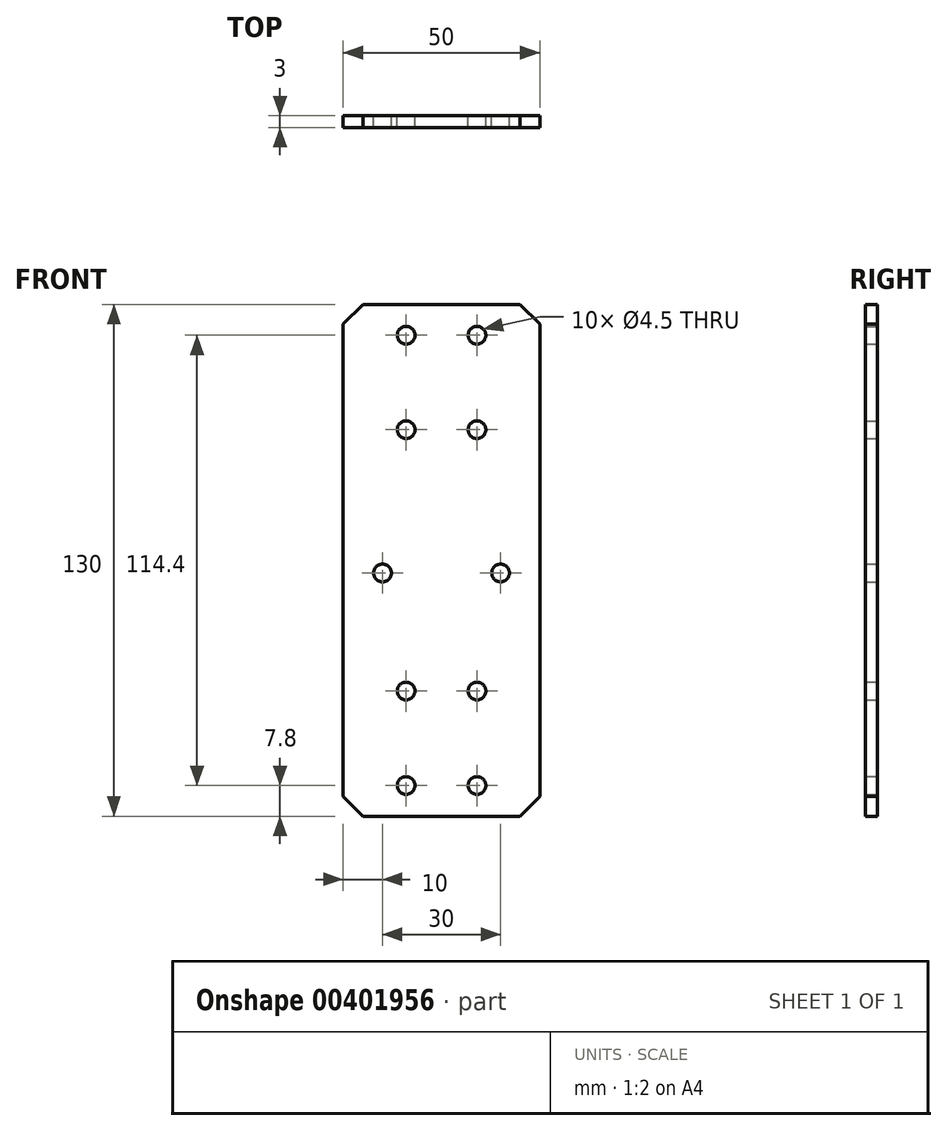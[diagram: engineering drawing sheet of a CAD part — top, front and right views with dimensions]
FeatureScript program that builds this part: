
annotation { "Feature Type Name" : "Feature", "Feature Type Description" : "" }
export const myFeature = defineFeature(function(context is Context, id is Id, definition is map)
    precondition{}
    {
        {
            var Q0;
            Q0=qCreatedBy(makeId("Front.planeOp"),FACE);
            var sketch = newSketch(context, id + "F0", { "sketchPlane" : qUnion([Q0])});
            skLineSegment(sketch, "E0.bottom", {"start": v(0, 0) * mm, "end": v(50, 0) * mm});
            skLineSegment(sketch, "E0.top", {"start": v(0, 130) * mm, "end": v(50, 130) * mm});
            skLineSegment(sketch, "E0.left", {"start": v(0, 0) * mm, "end": v(0, 130) * mm});
            skLineSegment(sketch, "E0.right", {"start": v(50, 0) * mm, "end": v(50, 130) * mm});
            skLineSegment(sketch, "E1", {"start": v(0, 65) * mm, "end": v(50, 65) * mm, "construction": true});
            skLineSegment(sketch, "E2", {"start": v(25, 130) * mm, "end": v(25, 65) * mm, "construction": true});
            skLineSegment(sketch, "E3", {"start": v(25, 65) * mm, "end": v(25, 0) * mm, "construction": true});
            skLineSegment(sketch, "E4", {"start": v(0, 110.2) * mm, "end": v(50, 110.2) * mm, "construction": true});
            skLineSegment(sketch, "E5.MirrorCS", {"start": v(0, 19.8) * mm, "end": v(50, 19.8) * mm, "construction": true});
            skLineSegment(sketch, "E6.bottom", {"start": v(16, 122.2) * mm, "end": v(34, 122.2) * mm, "construction": true});
            skLineSegment(sketch, "E6.top", {"start": v(16, 98.2) * mm, "end": v(34, 98.2) * mm, "construction": true});
            skLineSegment(sketch, "E6.left", {"start": v(16, 122.2) * mm, "end": v(16, 98.2) * mm, "construction": true});
            skLineSegment(sketch, "E6.right", {"start": v(34, 122.2) * mm, "end": v(34, 98.2) * mm, "construction": true});
            skPoint(sketch, "E7", {"position": v(25, 122.2) * mm});
            skPoint(sketch, "E8", {"position": v(16, 110.2) * mm});
            skLineSegment(sketch, "E9.MirrorCS", {"start": v(16, 31.8) * mm, "end": v(34, 31.8) * mm, "construction": true});
            skLineSegment(sketch, "E10.MirrorCS", {"start": v(34, 7.8) * mm, "end": v(34, 31.8) * mm, "construction": true});
            skLineSegment(sketch, "E11.MirrorCS", {"start": v(16, 7.8) * mm, "end": v(34, 7.8) * mm, "construction": true});
            skLineSegment(sketch, "E12.MirrorCS", {"start": v(16, 7.8) * mm, "end": v(16, 31.8) * mm, "construction": true});
            skCircle(sketch, "E13", {"center": v(16, 122.2) * mm, "radius": 2.25 * mm});
            skCircle(sketch, "E14", {"center": v(34, 122.2) * mm, "radius": 2.25 * mm});
            skCircle(sketch, "E15", {"center": v(34, 98.2) * mm, "radius": 2.25 * mm});
            skCircle(sketch, "E16", {"center": v(16, 98.2) * mm, "radius": 2.25 * mm});
            skCircle(sketch, "E17", {"center": v(16, 31.8) * mm, "radius": 2.25 * mm});
            skCircle(sketch, "E18", {"center": v(34, 31.8) * mm, "radius": 2.25 * mm});
            skCircle(sketch, "E19", {"center": v(16, 7.8) * mm, "radius": 2.25 * mm});
            skCircle(sketch, "E20", {"center": v(34, 7.8) * mm, "radius": 2.25 * mm});
            skLineSegment(sketch, "E21.bottom", {"start": v(10, 61.8) * mm, "end": v(40, 61.8) * mm, "construction": true});
            skLineSegment(sketch, "E21.top", {"start": v(10, 31.8) * mm, "end": v(40, 31.8) * mm, "construction": true});
            skLineSegment(sketch, "E21.left", {"start": v(10, 61.8) * mm, "end": v(10, 31.8) * mm, "construction": true});
            skLineSegment(sketch, "E21.right", {"start": v(40, 61.8) * mm, "end": v(40, 31.8) * mm, "construction": true});
            skPoint(sketch, "E22", {"position": v(25, 31.8) * mm});
            skCircle(sketch, "E23", {"center": v(40, 61.8) * mm, "radius": 2.25 * mm});
            skCircle(sketch, "E24", {"center": v(10, 61.8) * mm, "radius": 2.25 * mm});
            skSolve(sketch);
        }
        {
            var Q0;
            Q0 = qSketchRegion(id + "F0", true);
            extrude(context, id + "F1", {"entities" : qUnion([Q0]), "endBound" : BoundingType.SYMMETRIC, "depth" : 3 * mm});
        }
        {
            var Q0;
            Q0=makeQuery(id+"F1.opExtrude","SWEPT_EDGE",EDGE,{"disambiguationData":[OSD([sQuery(id+"F0.wireOp",EDGE,"E0.bottom"),sQuery(id+"F0.wireOp",EDGE,"E0.left")])]});
            var Q1;
            Q1=makeQuery(id+"F1.opExtrude","SWEPT_EDGE",EDGE,{"disambiguationData":[OSD([sQuery(id+"F0.wireOp",EDGE,"E0.bottom"),sQuery(id+"F0.wireOp",EDGE,"E0.right")])]});
            var Q2;
            Q2=makeQuery(id+"F1.opExtrude","SWEPT_EDGE",EDGE,{"disambiguationData":[OSD([sQuery(id+"F0.wireOp",EDGE,"E0.top"),sQuery(id+"F0.wireOp",EDGE,"E0.left")])]});
            var Q3;
            Q3=makeQuery(id+"F1.opExtrude","SWEPT_EDGE",EDGE,{"disambiguationData":[OSD([sQuery(id+"F0.wireOp",EDGE,"E0.top"),sQuery(id+"F0.wireOp",EDGE,"E0.right")])]});
            chamfer(context, id + "F2", {"entities" : qUnion([Q0, Q1, Q2, Q3]), "width" : 5 * mm, "tangentPropagation" : true});
        }
    });
